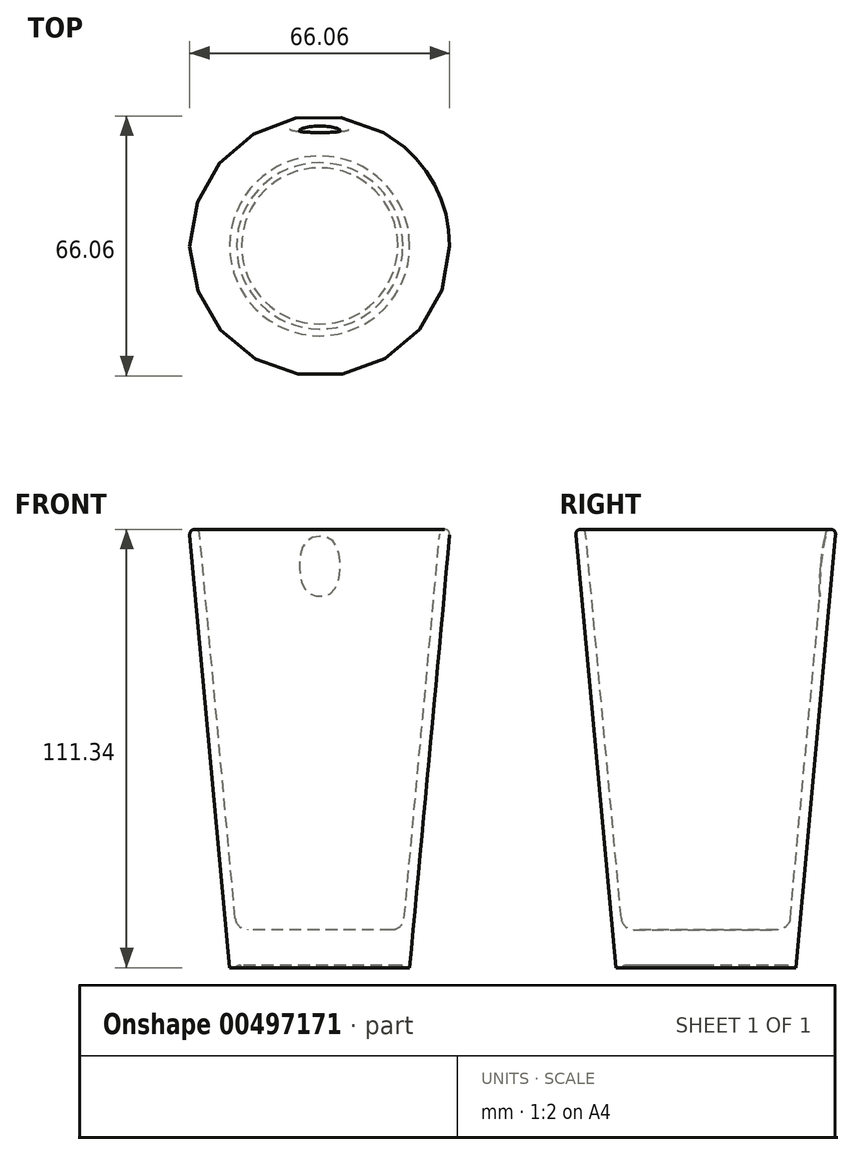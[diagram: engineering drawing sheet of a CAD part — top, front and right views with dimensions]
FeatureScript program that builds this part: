
annotation { "Feature Type Name" : "Feature", "Feature Type Description" : "" }
export const myFeature = defineFeature(function(context is Context, id is Id, definition is map)
    precondition{}
    {
        {
            var Q0;
            Q0=qCreatedBy(makeId("Front.planeOp"),FACE);
            var sketch = newSketch(context, id + "F0", { "sketchPlane" : qUnion([Q0])});
            skLineSegment(sketch, "E0", {"start": v(0, 0) * mm, "end": v(-19.85, 0) * mm});
            skLineSegment(sketch, "E1", {"start": v(-22.86, 0) * mm, "end": v(-33.02, 109.95) * mm});
            skLineSegment(sketch, "E2", {"start": v(0, 9.65) * mm, "end": v(0, 0) * mm});
            skLineSegment(sketch, "E3", {"start": v(0, 9.65) * mm, "end": v(-18.3, 9.65) * mm});
            skLineSegment(sketch, "E4.0", {"start": v(-21.47, 12.53) * mm, "end": v(-30.5, 110.18) * mm});
            skArc(sketch, "E5", {"start": v(-30.5, 110.18) * mm, "mid": v(-31.87, 111.33) * mm, "end": v(-33.02, 109.95) * mm});
            skArc(sketch, "E6.filletArc", {"start": v(-21.47, 12.53) * mm, "mid": v(-20.45, 10.48) * mm, "end": v(-18.3, 9.65) * mm});
            skPoint(sketch, "E7.orphan", {"position": v(0, 109.95) * mm});
            skArc(sketch, "E8", {"start": v(-19.85, 0) * mm, "mid": v(-20.48, 0.64) * mm, "end": v(-21.12, 0) * mm});
            skLineSegment(sketch, "E9.trimOffspring", {"start": v(-21.12, 0) * mm, "end": v(-22.86, 0) * mm});
            skSolve(sketch);
        }
        {
            var Q0;
            Q0 = qSketchRegion(id + "F0", true);
            var Q1;
            Q1=sQuery(id+"F0.wireOp",EDGE,"E2");
            revolve(context, id + "F1", {"entities" : qUnion([Q0]), "axis" : qUnion([Q1]), "revolveType" : RevolveType.FULL});
        }
        {
            var Q0;
            Q0=qCreatedBy(makeId("Right.planeOp"),FACE);
            var sketch = newSketch(context, id + "F2", { "sketchPlane" : qUnion([Q0])});
            skLineSegment(sketch, "E10", {"start": v(30.45, 109.53) * mm, "end": v(29.74, 101.94) * mm});
            skLineSegment(sketch, "E11", {"start": v(29.74, 101.94) * mm, "end": v(29.1, 102) * mm});
            skLineSegment(sketch, "E12", {"start": v(29.74, 101.94) * mm, "end": v(30.45, 109.53) * mm});
            skEllipticalArc(sketch, "E13", {});
            const initialGuessF2  = {"E13": [0.02974087931215763, 0.10194426029920578, 0.09253765640795626, 0.9957091855288487, 0.00762, 0.000635, 6.2831853071795845, 1.5707963267948961]};
            skSetInitialGuess(sketch, initialGuessF2);
            skSolve(sketch);
        }
        {
            var Q0;
            Q0 = qSketchRegion(id + "F2", true);
            var Q1;
            Q1=sQuery(id+"F2.wireOp",EDGE,"E11");
            revolve(context, id + "F3", {"operationType" : NewBodyOperationType.ADD, "entities" : qUnion([Q0]), "axis" : qUnion([Q1]), "revolveType" : RevolveType.FULL});
        }
        {
            var Q0;
            Q0=qCreatedBy(makeId("Front.planeOp"),FACE);
            var sketch = newSketch(context, id + "F4", { "sketchPlane" : qUnion([Q0])});
            skLineSegment(sketch, "E14", {"start": v(0, 0) * mm, "end": v(0, 125.14) * mm});
            skSolve(sketch);
        }
    });
